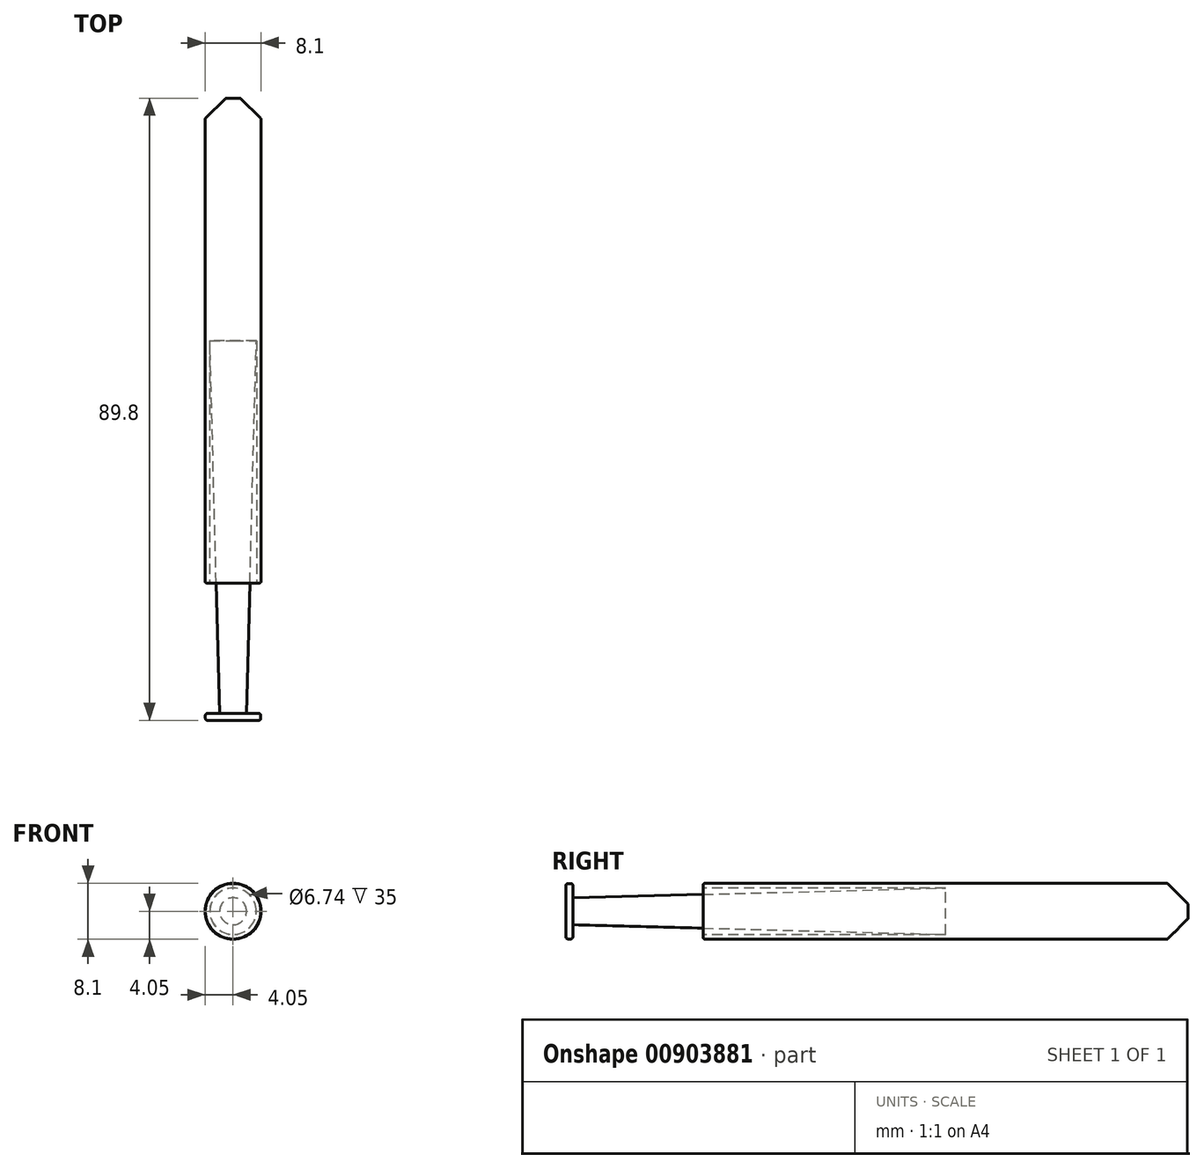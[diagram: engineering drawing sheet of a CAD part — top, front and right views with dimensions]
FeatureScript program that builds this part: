
annotation { "Feature Type Name" : "Feature", "Feature Type Description" : "" }
export const myFeature = defineFeature(function(context is Context, id is Id, definition is map)
    precondition{}
    {
        {
            var Q0;
            Q0=qCreatedBy(makeId("Front.planeOp"),FACE);
            var sketch = newSketch(context, id + "F0", { "sketchPlane" : qUnion([Q0])});
            skCircle(sketch, "E0", {"center": v(0, 0) * mm, "radius": 4.05 * mm});
            skSolve(sketch);
        }
        {
            var Q0;
            Q0=makeQuery(id+"F0.imprint","IMPRINT",FACE,{"disambiguationData":[TD([[makeQuery(id+"F0.imprint","IMPRINT",EDGE,{"derivedFrom":sQuery(id+"F0.wireOp",EDGE,"E0")}),1.0]])]});
            var Q1;
            Q1=sQuery(id+"F0.wireOp",EDGE,"E0");
            extrude(context, id + "F1", {"entities" : qUnion([Q0]), "surfaceEntities" : qUnion([Q1]), "depth" : 70 * mm, "offsetDistance" : 25 * mm});
        }
        {
            var Q0;
            Q0=makeQuery(id+"F1.opExtrude","CAP_EDGE",EDGE,{"disambiguationData":[OSD([sQuery(id+"F0.wireOp",EDGE,"E0")])],"isStart":true});
            chamfer(context, id + "F2", {"entities" : qUnion([Q0]), "width" : 3 * mm, "tangentPropagation" : true});
        }
        {
            var Q0;
            Q0=makeQuery(id+"F1.opExtrude","CAP_FACE",FACE,{"disambiguationData":[OSD([sQuery(id+"F0.wireOp",EDGE,"E0")])],"isStart":false});
            var sketch = newSketch(context, id + "F3", { "sketchPlane" : qUnion([Q0])});
            skCircle(sketch, "E1", {"center": v(0, 0) * mm, "radius": 3.37 * mm});
            skSolve(sketch);
        }
        {
            var Q0;
            Q0 = qSketchRegion(id + "F3", true);
            extrude(context, id + "F4", {"entities" : qUnion([Q0]), "operationType" : NewBodyOperationType.REMOVE, "oppositeDirection" : true, "depth" : 35 * mm, "offsetDistance" : 25 * mm});
        }
        {
            var Q0;
            Q0=makeQuery(id+"F4.boolean.opBoolean","COPY",FACE,{"derivedFrom":makeQuery(id+"F4.opExtrude","CAP_FACE",FACE,{"disambiguationData":[OSD([sQuery(id+"F3.wireOp",EDGE,"E1")])],"isStart":false})});
            var sketch = newSketch(context, id + "F5", { "sketchPlane" : qUnion([Q0])});
            skCircle(sketch, "E2", {"center": v(0, 0) * mm, "radius": 3.35 * mm});
            skSolve(sketch);
        }
        {
            var Q0;
            Q0 = qSketchRegion(id + "F5", true);
            extrude(context, id + "F6", {"entities" : qUnion([Q0]), "operationType" : NewBodyOperationType.ADD, "depth" : 53.8 * mm, "offsetDistance" : 25 * mm, "hasDraft" : true, "draftAngle" : 1.5 * degree, "draftPullDirection" : true});
        }
        {
            var Q0;
            Q0=makeQuery(id+"F6.opExtrude","CAP_FACE",FACE,{"disambiguationData":[OSD([sQuery(id+"F5.wireOp",EDGE,"E2")])],"isStart":false});
            var sketch = newSketch(context, id + "F7", { "sketchPlane" : qUnion([Q0])});
            skCircle(sketch, "E3", {"center": v(0, 0) * mm, "radius": 4 * mm});
            skSolve(sketch);
        }
        {
            var Q0;
            Q0 = qSketchRegion(id + "F7", true);
            extrude(context, id + "F8", {"entities" : qUnion([Q0]), "operationType" : NewBodyOperationType.ADD, "depth" : 1 * mm, "offsetDistance" : 25 * mm});
        }
        {
            var Q0;
            Q0=makeQuery(id+"F1.opExtrude","CAP_EDGE",EDGE,{"disambiguationData":[OSD([sQuery(id+"F0.wireOp",EDGE,"E0")])],"isStart":false});
            var Q1;
            {var subQ0=sQuery(id+"F0.wireOp",EDGE,"E0");Q1=makeQuery(id+"F2.opChamfer","BLEND_EDGE",EDGE,{"blendedFrom":[makeQuery(id+"F1.opExtrude","CAP_EDGE",EDGE,{"disambiguationData":[OSD([subQ0])],"isStart":true}),makeQuery(id+"F1.opExtrude","SWEPT_FACE",FACE,{"disambiguationData":[OSD([subQ0])]})],"blendedInto":[makeQuery(id+"F1.opExtrude","SWEPT_FACE",FACE,{"disambiguationData":[OSD([subQ0])]})]});}
            var Q2;
            {var subQ0=sQuery(id+"F0.wireOp",EDGE,"E0");Q2=makeQuery(id+"F2.opChamfer","BLEND_EDGE",EDGE,{"blendedFrom":[makeQuery(id+"F1.opExtrude","CAP_EDGE",EDGE,{"disambiguationData":[OSD([subQ0])],"isStart":true}),makeQuery(id+"F1.opExtrude","CAP_FACE",FACE,{"disambiguationData":[OSD([subQ0])],"isStart":true})],"blendedInto":[makeQuery(id+"F1.opExtrude","CAP_FACE",FACE,{"disambiguationData":[OSD([subQ0])],"isStart":true})]});}
            var Q3;
            Q3=makeQuery(id+"F6.opExtrude","CAP_EDGE",EDGE,{"disambiguationData":[OSD([sQuery(id+"F5.wireOp",EDGE,"E2")])],"isStart":false});
            var Q4;
            Q4=makeQuery(id+"F8.opExtrude","CAP_EDGE",EDGE,{"disambiguationData":[OSD([sQuery(id+"F7.wireOp",EDGE,"E3")])],"isStart":true});
            var Q5;
            Q5=makeQuery(id+"F8.opExtrude","CAP_EDGE",EDGE,{"disambiguationData":[OSD([sQuery(id+"F7.wireOp",EDGE,"E3")])],"isStart":false});
            fillet(context, id + "F9", {"entities" : qUnion([Q0, Q1, Q2, Q3, Q4, Q5]), "radius" : 0.3 * mm, "tangentPropagation" : true, "allowEdgeOverflow" : false});
        }
    });
